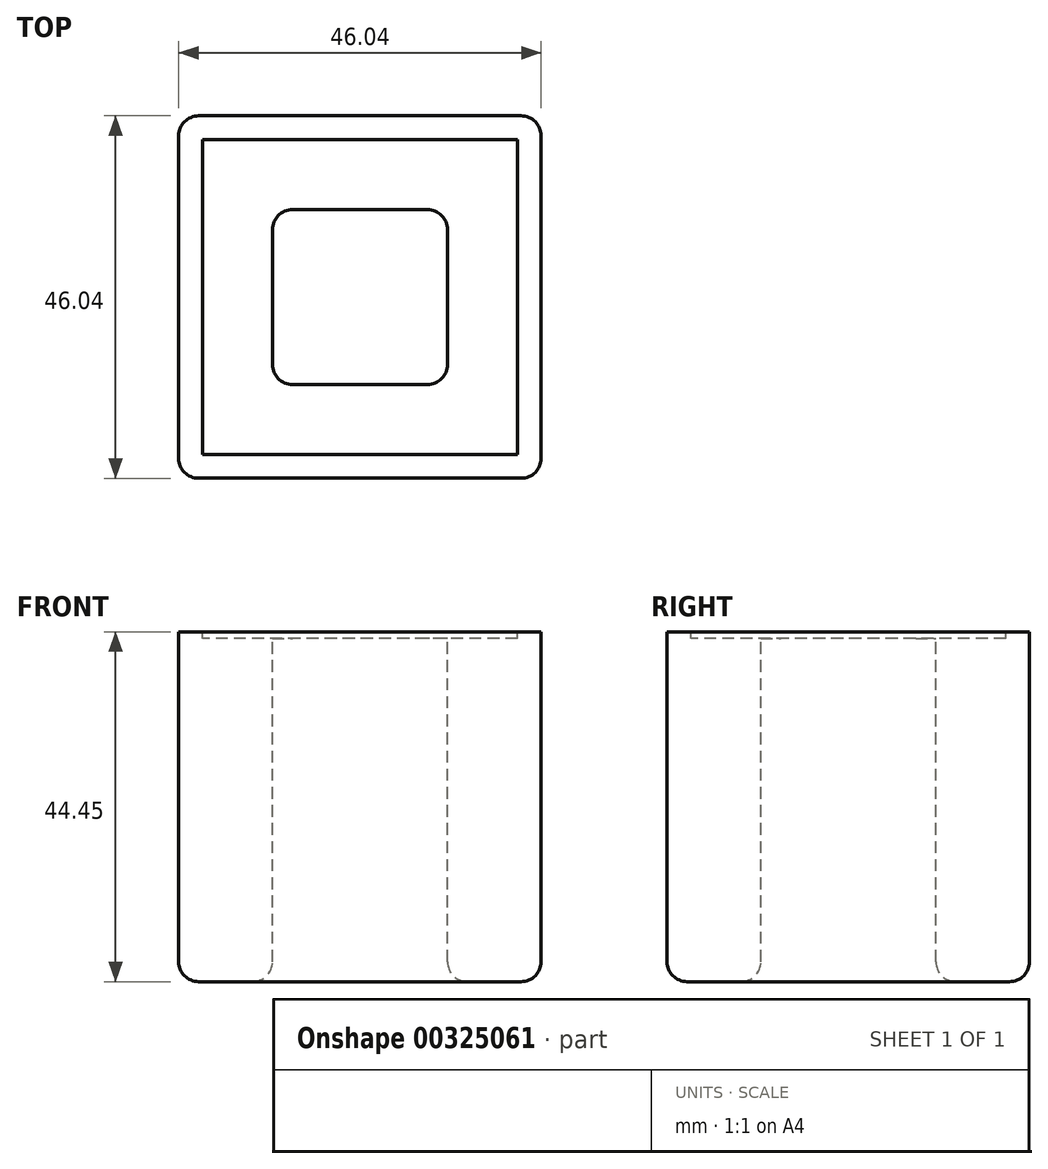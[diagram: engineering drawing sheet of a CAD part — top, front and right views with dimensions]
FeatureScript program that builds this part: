
annotation { "Feature Type Name" : "Feature", "Feature Type Description" : "" }
export const myFeature = defineFeature(function(context is Context, id is Id, definition is map)
    precondition{}
    {
        {
            var Q0;
            Q0=qCreatedBy(makeId("Top.planeOp"),FACE);
            var sketch = newSketch(context, id + "F0", { "sketchPlane" : qUnion([Q0])});
            skLineSegment(sketch, "E0.bottom", {"start": v(23.02, 23.02) * mm, "end": v(-23.02, 23.02) * mm});
            skLineSegment(sketch, "E0.top", {"start": v(23.02, -23.02) * mm, "end": v(-23.02, -23.02) * mm});
            skLineSegment(sketch, "E0.left", {"start": v(23.02, 23.02) * mm, "end": v(23.02, -23.02) * mm});
            skLineSegment(sketch, "E0.right", {"start": v(-23.02, 23.02) * mm, "end": v(-23.02, -23.02) * mm});
            skPoint(sketch, "E0.middle", {"position": v(0, 0) * mm});
            skSolve(sketch);
        }
        {
            var Q0;
            Q0 = qSketchRegion(id + "F0", true);
            extrude(context, id + "F1", {"entities" : qUnion([Q0]), "depth" : 44.45 * mm});
        }
        {
            var Q0;
            Q0=makeQuery(id+"F1.opExtrude","CAP_FACE",FACE,{"disambiguationData":[OSD([sQuery(id+"F0.wireOp",EDGE,"E0.bottom"),sQuery(id+"F0.wireOp",EDGE,"E0.top"),sQuery(id+"F0.wireOp",EDGE,"E0.left"),sQuery(id+"F0.wireOp",EDGE,"E0.right")])],"isStart":false});
            var sketch = newSketch(context, id + "F2", { "sketchPlane" : qUnion([Q0])});
            skLineSegment(sketch, "E1.bottom", {"start": v(20, 20) * mm, "end": v(-20, 20) * mm});
            skLineSegment(sketch, "E1.top", {"start": v(20, -20) * mm, "end": v(-20, -20) * mm});
            skLineSegment(sketch, "E1.left", {"start": v(20, 20) * mm, "end": v(20, -20) * mm});
            skLineSegment(sketch, "E1.right", {"start": v(-20, 20) * mm, "end": v(-20, -20) * mm});
            skPoint(sketch, "E1.middle", {"position": v(0, 0) * mm});
            skSolve(sketch);
        }
        {
            var Q0;
            Q0 = qSketchRegion(id + "F2", true);
            extrude(context, id + "F3", {"entities" : qUnion([Q0]), "operationType" : NewBodyOperationType.REMOVE, "oppositeDirection" : true, "depth" : ((3 / 4) + (1 / 8)) * mm});
        }
        {
            var Q0;
            Q0=makeQuery(id+"F3.boolean.opBoolean","COPY",FACE,{"derivedFrom":makeQuery(id+"F3.opExtrude","CAP_FACE",FACE,{"disambiguationData":[OSD([sQuery(id+"F2.wireOp",EDGE,"E1.bottom"),sQuery(id+"F2.wireOp",EDGE,"E1.top"),sQuery(id+"F2.wireOp",EDGE,"E1.left"),sQuery(id+"F2.wireOp",EDGE,"E1.right")])],"isStart":false})});
            var sketch = newSketch(context, id + "F4", { "sketchPlane" : qUnion([Q0])});
            skLineSegment(sketch, "E2.bottom", {"start": v(11.11, 11.11) * mm, "end": v(-11.11, 11.11) * mm});
            skLineSegment(sketch, "E2.top", {"start": v(11.11, -11.11) * mm, "end": v(-11.11, -11.11) * mm});
            skLineSegment(sketch, "E2.left", {"start": v(11.11, 11.11) * mm, "end": v(11.11, -11.11) * mm});
            skLineSegment(sketch, "E2.right", {"start": v(-11.11, 11.11) * mm, "end": v(-11.11, -11.11) * mm});
            skPoint(sketch, "E2.middle", {"position": v(0, 0) * mm});
            skSolve(sketch);
        }
        {
            var Q0;
            Q0 = qSketchRegion(id + "F4", true);
            extrude(context, id + "F5", {"entities" : qUnion([Q0]), "operationType" : NewBodyOperationType.REMOVE, "endBound" : BoundingType.THROUGH_ALL, "oppositeDirection" : true, "depth" : 25.4 * mm});
        }
        {
            var Q0;
            Q0=makeQuery(id+"F1.opExtrude","SWEPT_EDGE",EDGE,{"disambiguationData":[OSD([sQuery(id+"F0.wireOp",EDGE,"E0.bottom"),sQuery(id+"F0.wireOp",EDGE,"E0.right")])]});
            var Q1;
            Q1=makeQuery(id+"F1.opExtrude","SWEPT_EDGE",EDGE,{"disambiguationData":[OSD([sQuery(id+"F0.wireOp",EDGE,"E0.top"),sQuery(id+"F0.wireOp",EDGE,"E0.right")])]});
            var Q2;
            Q2=makeQuery(id+"F1.opExtrude","SWEPT_EDGE",EDGE,{"disambiguationData":[OSD([sQuery(id+"F0.wireOp",EDGE,"E0.top"),sQuery(id+"F0.wireOp",EDGE,"E0.left")])]});
            var Q3;
            Q3=makeQuery(id+"F1.opExtrude","SWEPT_EDGE",EDGE,{"disambiguationData":[OSD([sQuery(id+"F0.wireOp",EDGE,"E0.bottom"),sQuery(id+"F0.wireOp",EDGE,"E0.left")])]});
            var Q4;
            Q4=makeQuery(id+"F5.boolean.opBoolean","COPY",EDGE,{"derivedFrom":makeQuery(id+"F5.opExtrude","SWEPT_EDGE",EDGE,{"disambiguationData":[OSD([sQuery(id+"F4.wireOp",EDGE,"E2.top"),sQuery(id+"F4.wireOp",EDGE,"E2.right")])]})});
            var Q5;
            Q5=makeQuery(id+"F5.boolean.opBoolean","COPY",EDGE,{"derivedFrom":makeQuery(id+"F5.opExtrude","SWEPT_EDGE",EDGE,{"disambiguationData":[OSD([sQuery(id+"F4.wireOp",EDGE,"E2.bottom"),sQuery(id+"F4.wireOp",EDGE,"E2.right")])]})});
            var Q6;
            Q6=makeQuery(id+"F5.boolean.opBoolean","COPY",EDGE,{"derivedFrom":makeQuery(id+"F5.opExtrude","SWEPT_EDGE",EDGE,{"disambiguationData":[OSD([sQuery(id+"F4.wireOp",EDGE,"E2.bottom"),sQuery(id+"F4.wireOp",EDGE,"E2.left")])]})});
            var Q7;
            Q7=makeQuery(id+"F5.boolean.opBoolean","COPY",EDGE,{"derivedFrom":makeQuery(id+"F5.opExtrude","SWEPT_EDGE",EDGE,{"disambiguationData":[OSD([sQuery(id+"F4.wireOp",EDGE,"E2.top"),sQuery(id+"F4.wireOp",EDGE,"E2.left")])]})});
            var Q8;
            Q8=makeQuery(id+"F1.opExtrude","CAP_FACE",FACE,{"disambiguationData":[OSD([sQuery(id+"F0.wireOp",EDGE,"E0.bottom"),sQuery(id+"F0.wireOp",EDGE,"E0.top"),sQuery(id+"F0.wireOp",EDGE,"E0.left"),sQuery(id+"F0.wireOp",EDGE,"E0.right")])],"isStart":true});
            fillet(context, id + "F6", {"entities" : qUnion([Q0, Q1, Q2, Q3, Q4, Q5, Q6, Q7, Q8]), "radius" : 2.54 * mm, "tangentPropagation" : true, "allowEdgeOverflow" : false});
        }
    });
